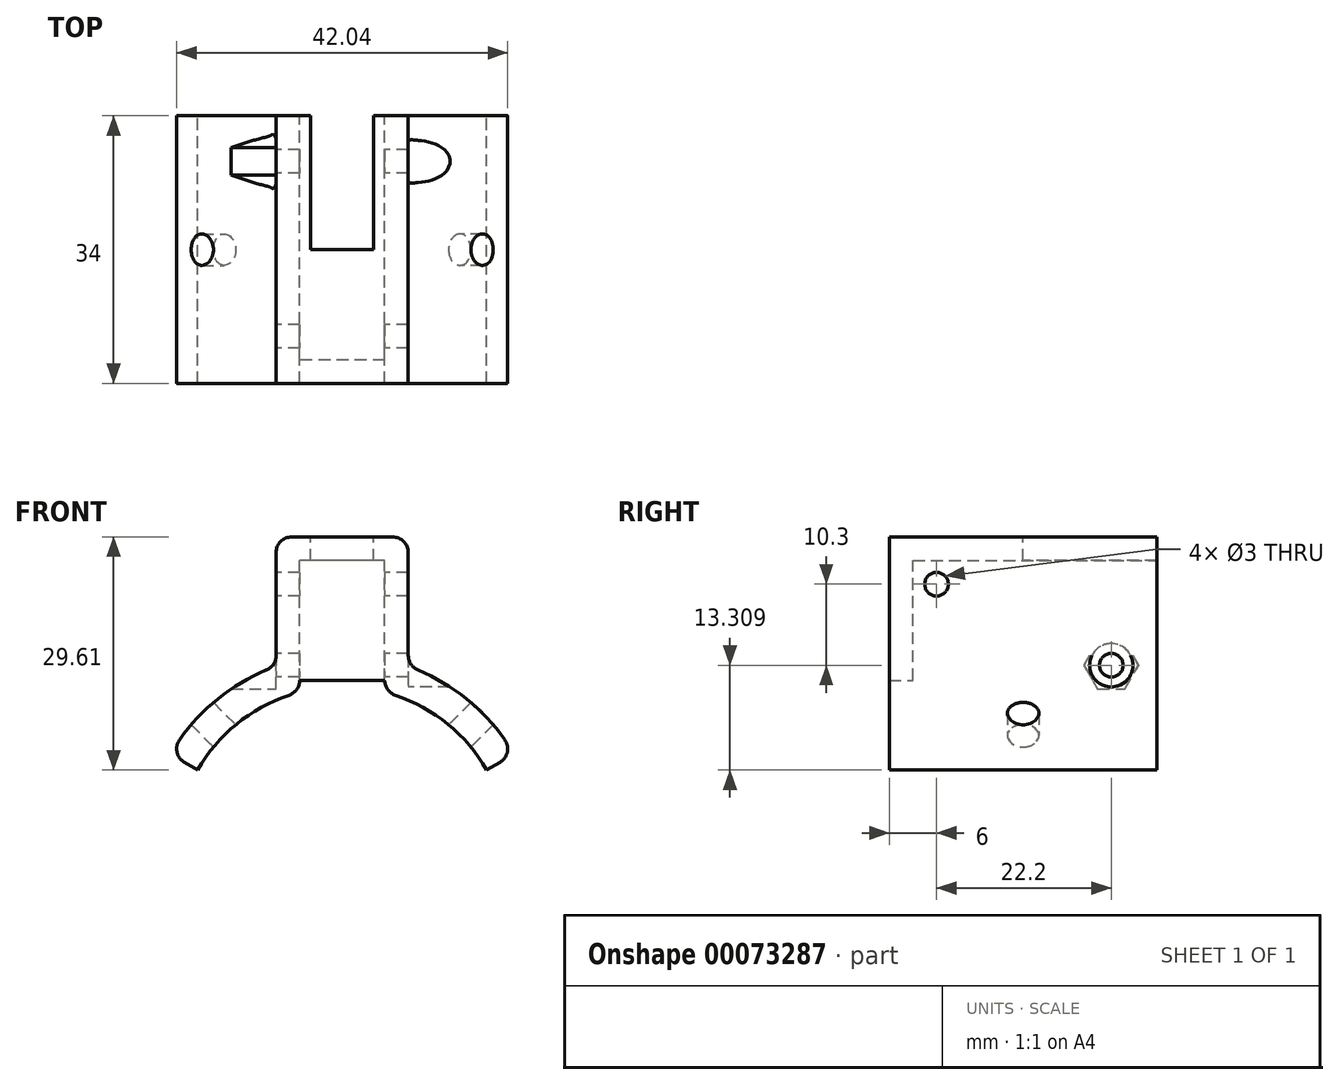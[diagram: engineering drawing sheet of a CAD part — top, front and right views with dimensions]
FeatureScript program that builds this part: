
annotation { "Feature Type Name" : "Feature", "Feature Type Description" : "" }
export const myFeature = defineFeature(function(context is Context, id is Id, definition is map)
    precondition{}
    {
        {
            var Q0;
            Q0=qCreatedBy(makeId("Front.planeOp"),FACE);
            var sketch = newSketch(context, id + "F0", { "sketchPlane" : qUnion([Q0])});
            skArc(sketch, "E0", {"start": v(18.37, 10.6) * mm, "mid": v(13.43, 16.41) * mm, "end": v(6.76, 20.1) * mm});
            skArc(sketch, "E1.0", {"start": v(20.66, 14.44) * mm, "mid": v(15.78, 19.66) * mm, "end": v(9.64, 23.3) * mm});
            skLineSegment(sketch, "E2", {"start": v(-18.37, 10.6) * mm, "end": v(-20.02, 11.56) * mm});
            skLineSegment(sketch, "E3", {"start": v(0, 0) * mm, "end": v(0, 21.2) * mm, "construction": true});
            skLineSegment(sketch, "E4.MirrorCS", {"start": v(18.37, 10.6) * mm, "end": v(20.02, 11.56) * mm});
            skLineSegment(sketch, "E5.rect.top", {"start": v(5.4, 37.2) * mm, "end": v(-5.4, 37.2) * mm});
            skLineSegment(sketch, "E5.rect.left", {"start": v(5.4, 22) * mm, "end": v(5.4, 37.2) * mm});
            skLineSegment(sketch, "E5.rect.right", {"start": v(-5.4, 22) * mm, "end": v(-5.4, 37.2) * mm});
            skPoint(sketch, "E5.rect.middle", {"position": v(0, 28.86) * mm});
            skArc(sketch, "E6.trimOffspring", {"start": v(-6.76, 20.1) * mm, "mid": v(-13.43, 16.41) * mm, "end": v(-18.37, 10.6) * mm});
            skArc(sketch, "E7.trimOffspring", {"start": v(-9.64, 23.3) * mm, "mid": v(-15.78, 19.66) * mm, "end": v(-20.66, 14.44) * mm});
            skLineSegment(sketch, "E8.0", {"start": v(8.4, 25.14) * mm, "end": v(8.4, 38.2) * mm});
            skLineSegment(sketch, "E8.1", {"start": v(6.4, 40.2) * mm, "end": v(-6.4, 40.2) * mm});
            skLineSegment(sketch, "E8.2", {"start": v(-8.4, 25.14) * mm, "end": v(-8.4, 38.2) * mm});
            skPoint(sketch, "E9.visualSharp", {"position": v(-8.4, 40.2) * mm});
            skArc(sketch, "E9.filletArc", {"start": v(-6.4, 40.2) * mm, "mid": v(-7.81, 39.62) * mm, "end": v(-8.4, 38.2) * mm});
            skPoint(sketch, "E10.visualSharp", {"position": v(8.4, 40.2) * mm});
            skArc(sketch, "E10.filletArc", {"start": v(8.4, 38.2) * mm, "mid": v(7.81, 39.62) * mm, "end": v(6.4, 40.2) * mm});
            skPoint(sketch, "E11.visualSharp", {"position": v(8.4, 23.77) * mm});
            skArc(sketch, "E11.filletArc", {"start": v(8.4, 25.14) * mm, "mid": v(8.74, 24.03) * mm, "end": v(9.64, 23.3) * mm});
            skPoint(sketch, "E12.visualSharp", {"position": v(-8.4, 23.77) * mm});
            skArc(sketch, "E12.filletArc", {"start": v(-9.64, 23.3) * mm, "mid": v(-8.74, 24.03) * mm, "end": v(-8.4, 25.14) * mm});
            skPoint(sketch, "E13.visualSharp", {"position": v(-21.83, 12.6) * mm});
            skArc(sketch, "E13.filletArc", {"start": v(-20.66, 14.44) * mm, "mid": v(-20.98, 12.86) * mm, "end": v(-20.02, 11.56) * mm});
            skPoint(sketch, "E14.visualSharp", {"position": v(-5.4, 20.51) * mm});
            skArc(sketch, "E14.filletArc", {"start": v(-6.76, 20.1) * mm, "mid": v(-5.78, 20.83) * mm, "end": v(-5.4, 22) * mm});
            skPoint(sketch, "E15.visualSharp", {"position": v(5.4, 20.51) * mm});
            skArc(sketch, "E15.filletArc", {"start": v(5.4, 22) * mm, "mid": v(5.78, 20.83) * mm, "end": v(6.76, 20.1) * mm});
            skPoint(sketch, "E16.visualSharp", {"position": v(21.83, 12.6) * mm});
            skArc(sketch, "E16.filletArc", {"start": v(20.02, 11.56) * mm, "mid": v(20.98, 12.86) * mm, "end": v(20.66, 14.44) * mm});
            skSolve(sketch);
        }
        {
            var Q0;
            Q0=makeQuery(id+"F0.imprint","IMPRINT",FACE,{"disambiguationData":[TD([[makeQuery(id+"F0.imprint","IMPRINT",EDGE,{"derivedFrom":sQuery(id+"F0.wireOp",EDGE,"E0")}),-1.0]])]});
            extrude(context, id + "F1", {"entities" : qUnion([Q0]), "endBound" : BoundingType.SYMMETRIC, "depth" : 34 * mm});
        }
        {
            var Q0;
            Q0=makeQuery(id+"F1.opExtrude","CAP_FACE",FACE,{"disambiguationData":[OSD([sQuery(id+"F0.wireOp",EDGE,"E0"),sQuery(id+"F0.wireOp",EDGE,"E1.0"),sQuery(id+"F0.wireOp",EDGE,"E2"),sQuery(id+"F0.wireOp",EDGE,"E4.MirrorCS"),sQuery(id+"F0.wireOp",EDGE,"E5.rect.top"),sQuery(id+"F0.wireOp",EDGE,"E5.rect.left"),sQuery(id+"F0.wireOp",EDGE,"E5.rect.right"),sQuery(id+"F0.wireOp",EDGE,"E6.trimOffspring"),sQuery(id+"F0.wireOp",EDGE,"E7.trimOffspring"),sQuery(id+"F0.wireOp",EDGE,"E8.0"),sQuery(id+"F0.wireOp",EDGE,"E8.1"),sQuery(id+"F0.wireOp",EDGE,"E8.2"),sQuery(id+"F0.wireOp",EDGE,"E9.filletArc"),sQuery(id+"F0.wireOp",EDGE,"E10.filletArc"),sQuery(id+"F0.wireOp",EDGE,"E11.filletArc"),sQuery(id+"F0.wireOp",EDGE,"E12.filletArc"),sQuery(id+"F0.wireOp",EDGE,"E13.filletArc"),sQuery(id+"F0.wireOp",EDGE,"E14.filletArc"),sQuery(id+"F0.wireOp",EDGE,"E15.filletArc"),sQuery(id+"F0.wireOp",EDGE,"E16.filletArc")])],"isStart":false});
            var sketch = newSketch(context, id + "F2", { "sketchPlane" : qUnion([Q0])});
            skLineSegment(sketch, "E17.bottom", {"start": v(-5.4, 37.2) * mm, "end": v(5.4, 37.2) * mm});
            skLineSegment(sketch, "E17.top", {"start": v(-5.4, 22) * mm, "end": v(5.4, 22) * mm});
            skLineSegment(sketch, "E17.left", {"start": v(-5.4, 37.2) * mm, "end": v(-5.4, 22) * mm});
            skLineSegment(sketch, "E17.right", {"start": v(5.4, 37.2) * mm, "end": v(5.4, 22) * mm});
            skSolve(sketch);
        }
        {
            var Q0;
            Q0=makeQuery(id+"F2.imprint","IMPRINT",FACE,{"disambiguationData":[TD([[makeQuery(id+"F2.imprint","IMPRINT",EDGE,{"derivedFrom":sQuery(id+"F2.wireOp",EDGE,"E17.bottom")}),1.0]])]});
            extrude(context, id + "F3", {"entities" : qUnion([Q0]), "operationType" : NewBodyOperationType.ADD, "oppositeDirection" : true, "depth" : 3 * mm});
        }
        {
            var Q0;
            Q0=makeQuery(id+"F1.opExtrude","SWEPT_FACE",FACE,{"disambiguationData":[OSD([sQuery(id+"F0.wireOp",EDGE,"E5.rect.left")])]});
            var sketch = newSketch(context, id + "F4", { "sketchPlane" : qUnion([Q0])});
            skCircle(sketch, "E18", {"center": v(11, 34.2) * mm, "radius": 1.5 * mm});
            skCircle(sketch, "E19", {"center": v(-11.2, 23.9) * mm, "radius": 1.5 * mm});
            skSolve(sketch);
        }
        {
            var Q0;
            Q0=makeQuery(id+"F4.imprint","IMPRINT",FACE,{"disambiguationData":[TD([[makeQuery(id+"F4.imprint","IMPRINT",EDGE,{"derivedFrom":sQuery(id+"F4.wireOp",EDGE,"E19")}),1.0]])]});
            var Q1;
            Q1=makeQuery(id+"F4.imprint","IMPRINT",FACE,{"disambiguationData":[TD([[makeQuery(id+"F4.imprint","IMPRINT",EDGE,{"derivedFrom":sQuery(id+"F4.wireOp",EDGE,"E18")}),1.0]])]});
            extrude(context, id + "F5", {"entities" : qUnion([Q0, Q1]), "operationType" : NewBodyOperationType.REMOVE, "endBound" : BoundingType.SYMMETRIC, "oppositeDirection" : true, "depth" : 40 * mm});
        }
        {
            var Q0;
            Q0=qCreatedBy(makeId("Top.planeOp"),FACE);
            var sketch = newSketch(context, id + "F6", { "sketchPlane" : qUnion([Q0])});
            skLineSegment(sketch, "E20", {"start": v(0, 43.5) * mm, "end": v(0, -50.44) * mm, "construction": true});
            skSolve(sketch);
        }
        {
            var Q0;
            Q0=sQuery(id+"F6.wireOp",EDGE,"E20");
            cPlane(context, id + "F7", {"entities" : qUnion([Q0]), "cplaneType" : CPlaneType.LINE_ANGLE, "offset" : 150 * mm, "angle" : 45 * degree, "width" : 150 * mm, "height" : 150 * mm});
        }
        {
            var Q0;
            Q0=qCreatedBy(id+"F7.planeOp",FACE);
            var sketch = newSketch(context, id + "F8", { "sketchPlane" : qUnion([Q0])});
            skCircle(sketch, "E21", {"center": v(0, 0) * mm, "radius": 2 * mm});
            skArc(sketch, "E22", {"start": v(-5.72, 1.8) * mm, "mid": v(-5.93, 0.91) * mm, "end": v(-6, 0) * mm});
            skLineSegment(sketch, "E23", {"start": v(-5.72, 1.8) * mm, "end": v(0, 19.99) * mm});
            skLineSegment(sketch, "E24", {"start": v(0, 19.99) * mm, "end": v(0, 24.74) * mm});
            skLineSegment(sketch, "E25", {"start": v(0, 24.74) * mm, "end": v(-12.49, 24.74) * mm});
            skLineSegment(sketch, "E26", {"start": v(-12.49, 24.74) * mm, "end": v(-12.49, 0) * mm});
            skLineSegment(sketch, "E27", {"start": v(0, 0) * mm, "end": v(-6, 0) * mm, "construction": true});
            skArc(sketch, "E28.MirrorCS", {"start": v(-5.72, -1.8) * mm, "mid": v(-5.93, -0.91) * mm, "end": v(-6, 0) * mm});
            skLineSegment(sketch, "E29.MirrorCS", {"start": v(-5.72, -1.8) * mm, "end": v(0, -19.99) * mm});
            skLineSegment(sketch, "E30.MirrorCS", {"start": v(0, -19.99) * mm, "end": v(0, -24.74) * mm});
            skLineSegment(sketch, "E31.MirrorCS", {"start": v(0, -24.74) * mm, "end": v(-12.49, -24.74) * mm});
            skLineSegment(sketch, "E32.MirrorCS", {"start": v(-12.49, -24.74) * mm, "end": v(-12.49, 0) * mm});
            skSolve(sketch);
        }
        {
            var Q0;
            Q0=makeQuery(id+"F8.imprint","IMPRINT",FACE,{"disambiguationData":[TD([[makeQuery(id+"F8.imprint","IMPRINT",EDGE,{"derivedFrom":sQuery(id+"F8.wireOp",EDGE,"E21")}),1.0]])]});
            var Q1;
            Q1=sQuery(id+"F8.wireOp",EDGE,"E21");
            extrude(context, id + "F9", {"entities" : qUnion([Q0]), "operationType" : NewBodyOperationType.REMOVE, "surfaceEntities" : qUnion([Q1]), "endBound" : BoundingType.THROUGH_ALL, "oppositeDirection" : true, "depth" : 25 * mm});
        }
        {
            var Q0;
            Q0=qCreatedBy(makeId("Top.planeOp"),FACE);
            var Q1;
            Q1=sQuery(id+"F6.wireOp",EDGE,"E20");
            cPlane(context, id + "F10", {"entities" : qUnion([Q0, Q1]), "cplaneType" : CPlaneType.LINE_ANGLE, "offset" : 150 * mm, "angle" : 135 * degree, "width" : 150 * mm, "height" : 150 * mm});
        }
        {
            var Q0;
            Q0=qCreatedBy(id+"F10.planeOp",FACE);
            var sketch = newSketch(context, id + "F11", { "sketchPlane" : qUnion([Q0])});
            skCircle(sketch, "E33", {"center": v(0, 0) * mm, "radius": 2 * mm});
            skSolve(sketch);
        }
        {
            var Q0;
            Q0=makeQuery(id+"F11.imprint","IMPRINT",FACE,{"disambiguationData":[TD([[makeQuery(id+"F11.imprint","IMPRINT",EDGE,{"derivedFrom":sQuery(id+"F11.wireOp",EDGE,"E33")}),1.0]])]});
            extrude(context, id + "F12", {"entities" : qUnion([Q0]), "operationType" : NewBodyOperationType.REMOVE, "endBound" : BoundingType.THROUGH_ALL, "depth" : 25 * mm});
        }
        {
            var Q0;
            Q0=makeQuery(id+"F1.opExtrude","SWEPT_FACE",FACE,{"disambiguationData":[OSD([sQuery(id+"F0.wireOp",EDGE,"E8.1")])]});
            var sketch = newSketch(context, id + "F13", { "sketchPlane" : qUnion([Q0])});
            skLineSegment(sketch, "E34.bottom", {"start": v(-4, 0) * mm, "end": v(4, 0) * mm});
            skLineSegment(sketch, "E34.top", {"start": v(-4, 17) * mm, "end": v(4, 17) * mm});
            skLineSegment(sketch, "E34.left", {"start": v(-4, 0) * mm, "end": v(-4, 17) * mm});
            skLineSegment(sketch, "E34.right", {"start": v(4, 0) * mm, "end": v(4, 17) * mm});
            skSolve(sketch);
        }
        {
            var Q0;
            Q0=makeQuery(id+"F1.opExtrude","SWEPT_FACE",FACE,{"disambiguationData":[OSD([sQuery(id+"F0.wireOp",EDGE,"E8.0")])]});
            var sketch = newSketch(context, id + "F14", { "sketchPlane" : qUnion([Q0])});
            skCircle(sketch, "E35", {"center": v(11.2, 23.9) * mm, "radius": 2.75 * mm});
            skSolve(sketch);
        }
        {
            var Q0;
            {var subQ11=sQuery(id+"F0.wireOp",EDGE,"E8.0");var subQ22=makeQuery(id+"F1.opExtrude","SWEPT_FACE",FACE,{"disambiguationData":[OSD([subQ11])]});var subQ23=makeQuery(id+"F5.opExtrude","SWEPT_FACE",FACE,{"disambiguationData":[OSD([sQuery(id+"F4.wireOp",EDGE,"E19")])]});var subQ29=makeQuery(id+"F5.boolean.opBoolean","INTERSECT",EDGE,{"derivedFrom":[subQ22,subQ23]});Q0=makeQuery(id+"F14.imprint","IMPRINT",FACE,{"disambiguationData":[TD([[makeQuery(id+"F14.imprint","IMPRINT",EDGE,{"derivedFrom":subQ29}),1.0]])]});}
            var Q1;
            {var subQ11=sQuery(id+"F0.wireOp",EDGE,"E8.0");var subQ22=makeQuery(id+"F1.opExtrude","SWEPT_FACE",FACE,{"disambiguationData":[OSD([subQ11])]});var subQ23=makeQuery(id+"F5.opExtrude","SWEPT_FACE",FACE,{"disambiguationData":[OSD([sQuery(id+"F4.wireOp",EDGE,"E19")])]});var subQ29=makeQuery(id+"F5.boolean.opBoolean","INTERSECT",EDGE,{"derivedFrom":[subQ22,subQ23]});Q1=makeQuery(id+"F14.imprint","IMPRINT",FACE,{"disambiguationData":[TD([[makeQuery(id+"F14.imprint","IMPRINT",EDGE,{"derivedFrom":subQ29}),-1.0]])]});}
            extrude(context, id + "F15", {"entities" : qUnion([Q0, Q1]), "operationType" : NewBodyOperationType.REMOVE, "depth" : 25 * mm});
        }
        {
            var Q0;
            Q0=makeQuery(id+"F1.opExtrude","SWEPT_FACE",FACE,{"disambiguationData":[OSD([sQuery(id+"F0.wireOp",EDGE,"E8.2")])]});
            var sketch = newSketch(context, id + "F16", { "sketchPlane" : qUnion([Q0])});
            skCircle(sketch, "E36.cCircle", {"center": v(-11.2, 23.9) * mm, "radius": 3 * mm, "construction": true});
            skPoint(sketch, "E36.cCircle.perimeterSnap0", {"position": v(-11.2, 25.4) * mm});
            skLineSegment(sketch, "E36.0", {"start": v(-12.93, 26.9) * mm, "end": v(-9.47, 26.9) * mm});
            skLineSegment(sketch, "E36.1", {"start": v(-9.47, 26.9) * mm, "end": v(-7.74, 23.9) * mm});
            skLineSegment(sketch, "E36.2", {"start": v(-7.74, 23.9) * mm, "end": v(-9.47, 20.9) * mm});
            skLineSegment(sketch, "E36.3", {"start": v(-9.47, 20.9) * mm, "end": v(-12.93, 20.9) * mm});
            skLineSegment(sketch, "E36.4", {"start": v(-12.93, 20.9) * mm, "end": v(-14.66, 23.9) * mm});
            skLineSegment(sketch, "E36.5", {"start": v(-14.66, 23.9) * mm, "end": v(-12.93, 26.9) * mm});
            skPoint(sketch, "E36.0.midPoint", {"position": v(-11.2, 26.9) * mm});
            skPoint(sketch, "E36.0.midPoint.positionSnap0", {"position": v(-11.2, 25.4) * mm});
            skSolve(sketch);
        }
        {
            var Q0;
            {var subQ0=sQuery(id+"F16.wireOp",EDGE,"E36.2");Q0=makeQuery(id+"F16.imprint","IMPRINT",FACE,{"disambiguationData":[TD([[makeQuery(id+"F16.imprint","IMPRINT",EDGE,{"derivedFrom":subQ0}),-1.0]])]});}
            extrude(context, id + "F17", {"entities" : qUnion([Q0]), "operationType" : NewBodyOperationType.REMOVE, "depth" : 25 * mm});
        }
        {
            var Q0;
            Q0=makeQuery(id+"F13.imprint","IMPRINT",FACE,{"disambiguationData":[TD([[makeQuery(id+"F13.imprint","IMPRINT",EDGE,{"derivedFrom":sQuery(id+"F13.wireOp",EDGE,"E34.bottom")}),1.0]])]});
            extrude(context, id + "F18", {"entities" : qUnion([Q0]), "operationType" : NewBodyOperationType.REMOVE, "oppositeDirection" : true, "depth" : 25 * mm});
        }
    });
